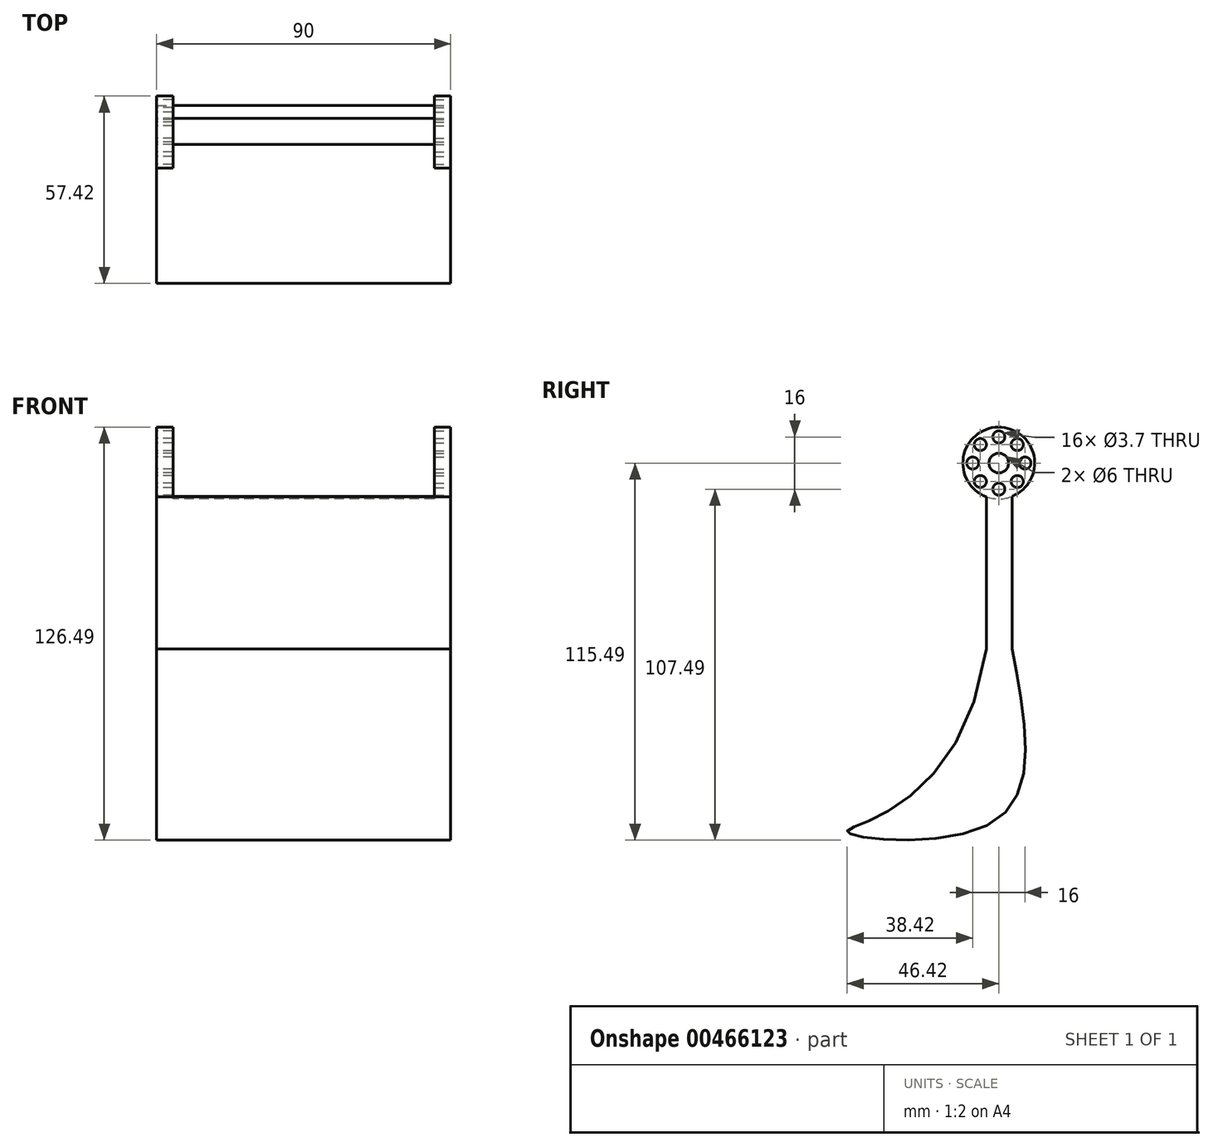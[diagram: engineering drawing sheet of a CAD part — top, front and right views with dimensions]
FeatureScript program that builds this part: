
annotation { "Feature Type Name" : "Feature", "Feature Type Description" : "" }
export const myFeature = defineFeature(function(context is Context, id is Id, definition is map)
    precondition{}
    {
        {
            var Q0;
            Q0=qCreatedBy(makeId("Right.planeOp"),FACE);
            var sketch = newSketch(context, id + "F0", { "sketchPlane" : qUnion([Q0])});
            skCircle(sketch, "E0", {"center": v(0, 0) * mm, "radius": 11 * mm});
            skCircle(sketch, "E1", {"center": v(0, 0) * mm, "radius": 3 * mm});
            skCircle(sketch, "E2", {"center": v(0, 8) * mm, "radius": 1.85 * mm});
            skCircle(sketch, "E3.1.0", {"center": v(-5.66, 5.66) * mm, "radius": 1.85 * mm});
            skCircle(sketch, "E3.2.0", {"center": v(-8, 0) * mm, "radius": 1.85 * mm});
            skCircle(sketch, "E3.3.0", {"center": v(-5.66, -5.66) * mm, "radius": 1.85 * mm});
            skCircle(sketch, "E4.1.4.0", {"center": v(0, -8) * mm, "radius": 1.85 * mm});
            skCircle(sketch, "E4.1.5.0", {"center": v(5.66, -5.66) * mm, "radius": 1.85 * mm});
            skCircle(sketch, "E4.1.6.0", {"center": v(8, 0) * mm, "radius": 1.85 * mm});
            skCircle(sketch, "E4.1.7.0", {"center": v(5.66, 5.66) * mm, "radius": 1.85 * mm});
            skLineSegment(sketch, "E5", {"start": v(-3.85, -10.11) * mm, "end": v(-3.85, -57) * mm});
            skLineSegment(sketch, "E6", {"start": v(-3.85, -57) * mm, "end": v(4.15, -57) * mm});
            skLineSegment(sketch, "E7", {"start": v(4.15, -57) * mm, "end": v(4.15, -10.19) * mm});
            skPoint(sketch, "E8.1.internal.snap0", {"position": v(0.15, -57) * mm});
            skFitSpline(sketch, "E9", {"points": [v(4.15, -57) * mm, v(0, -108.77) * mm, v(-46.18, -113.25) * mm, v(-3.85, -57) * mm], "startDerivative": vector(25.87, -160.67) * mm, "endDerivative": vector(60.85, 414.77) * mm});
            skSolve(sketch);
        }
        {
            var Q0;
            {var subQ4=sQuery(id+"F0.wireOp",EDGE,"E6");Q0=makeQuery(id+"F0.imprint","IMPRINT",FACE,{"disambiguationData":[TD([[makeQuery(id+"F0.imprint","IMPRINT",EDGE,{"derivedFrom":subQ4}),1.0]])]});}
            var Q1;
            Q1=makeQuery(id+"F0.imprint","IMPRINT",FACE,{"disambiguationData":[TD([[makeQuery(id+"F0.imprint","IMPRINT",EDGE,{"derivedFrom":sQuery(id+"F0.wireOp",EDGE,"E6")}),-1.0]])]});
            extrude(context, id + "F1", {"entities" : qUnion([Q0, Q1]), "depth" : 45 * mm});
        }
        {
            var Q0;
            Q0=makeQuery(id+"F0.imprint","IMPRINT",FACE,{"disambiguationData":[TD([[makeQuery(id+"F0.imprint","IMPRINT",EDGE,{"derivedFrom":sQuery(id+"F0.wireOp",EDGE,"E1")}),-1.0]])]});
            extrude(context, id + "F2", {"entities" : qUnion([Q0]), "operationType" : NewBodyOperationType.ADD, "depth" : 5 * mm});
        }
        {
            var Q0;
            Q0=makeQuery(id+"F1.opExtrude","SWEPT_BODY",BODY,{"disambiguationData":[OSD([sQuery(id+"F0.wireOp",EDGE,"E0"),sQuery(id+"F0.wireOp",EDGE,"E5"),sQuery(id+"F0.wireOp",EDGE,"E7"),sQuery(id+"F0.wireOp",EDGE,"E9")])]});
            var Q1;
            Q1=makeQuery(id+"F1.opExtrude","CAP_FACE",FACE,{"disambiguationData":[OSD([sQuery(id+"F0.wireOp",EDGE,"E0"),sQuery(id+"F0.wireOp",EDGE,"E5"),sQuery(id+"F0.wireOp",EDGE,"E7"),sQuery(id+"F0.wireOp",EDGE,"E9")])],"isStart":false});
            mirror(context, id + "F3", {"operationType" : NewBodyOperationType.ADD, "entities" : qUnion([Q0]), "mirrorPlane" : qUnion([Q1])});
        }
    });
